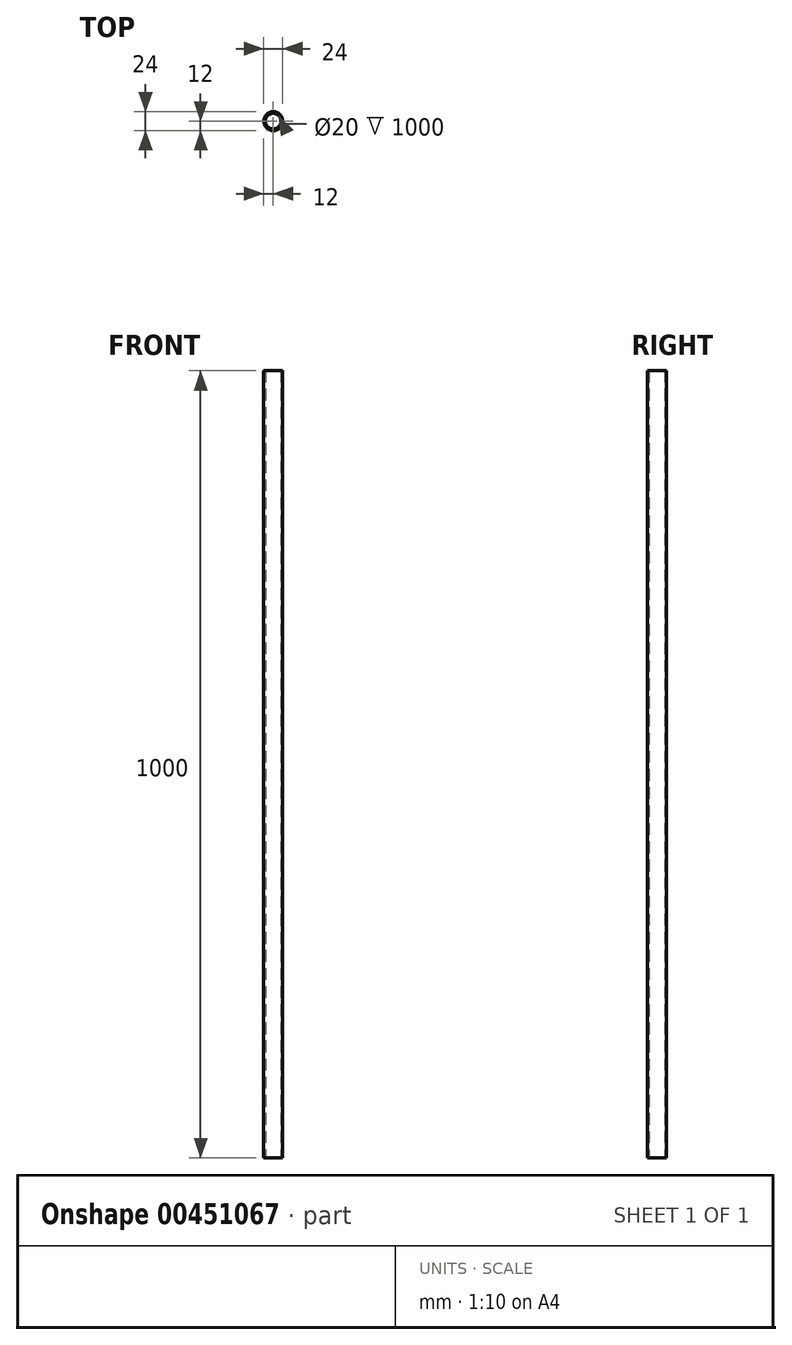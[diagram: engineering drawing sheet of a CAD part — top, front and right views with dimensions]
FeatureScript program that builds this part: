
annotation { "Feature Type Name" : "Feature", "Feature Type Description" : "" }
export const myFeature = defineFeature(function(context is Context, id is Id, definition is map)
    precondition{}
    {
        {
            var Q0;
            Q0=qCreatedBy(makeId("Top.planeOp"),FACE);
            var sketch = newSketch(context, id + "F0", { "sketchPlane" : qUnion([Q0])});
            skCircle(sketch, "E0", {"center": v(0, 0) * mm, "radius": 12 * mm});
            skCircle(sketch, "E1", {"center": v(0, 0) * mm, "radius": 10 * mm});
            skSolve(sketch);
        }
        {
            var Q0;
            Q0=makeQuery(id+"F0.imprint","IMPRINT",FACE,{"disambiguationData":[TD([[makeQuery(id+"F0.imprint","IMPRINT",EDGE,{"derivedFrom":sQuery(id+"F0.wireOp",EDGE,"E0")}),1.0]])]});
            extrude(context, id + "F1", {"entities" : qUnion([Q0]), "depth" : 1000 * mm});
        }
    });
